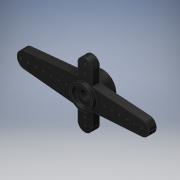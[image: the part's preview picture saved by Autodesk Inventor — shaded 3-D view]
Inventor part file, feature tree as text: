
AUTODESK INVENTOR PART (.ipt)
format: ipt  version: 2018 (Build 220112000, 112)  size: 246,784 bytes
history: native  units: in
note: dims shown in document units (in); Inventor stores cm internally (conversion verified against a paired STEP export)
features: extrude x6, sketch x6, fillet x3
ambient origin geometry x8: Origin, YZ Plane, XZ Plane, XY Plane, X Axis, Y Axis, Z Axis, Center Point
bodies: Solid1 (feature_tree)
feature tree (15):
  extrude  "Horn_Body"  Depth=0.6693in
  fillet  "Fillet1"  Radius=0.2234in
  fillet  "Fillet2"  Radius=0.2234in
  fillet  "Fillet3"  Radius=0.5118in
  extrude  "Shaft_Connector"  Depth=0.5906in
  extrude  "Shaft_Opening"  Depth=0.1969in
  extrude  "Opening_Horn_FixationScrew"  Depth=0.5906in
  extrude  "Connection_Holes"  Depth=0.6299in
  extrude  "Centering_RIng"  Depth=0.0787in TaperAngle=0.0deg
  sketch  "Sketch1"  dims[d0=0.1496in d1=0.6693in d2=0.2234in d3=0.2234in d4=0.5118in]
  sketch  "Sketch2"  dims[d5=0.1535in d8=0.5906in]
  sketch  "Sketch3"  dims[d9=0.5906in d10=0.1969in]
  sketch  "Sketch4"  dims[d11=0.1969in d12=0.5906in]
  sketch  "Sketch6"  dims[d13=0.1575in d14=0.6299in]
  sketch  "Sketch8"  dims[d15=0.6299in d16=0.0787in d17=0.0in d18=0.0748in d19=0.0748in d20=0.0787in d21=0.2795in d22=0.1496in d23=0.0748in d24=0.1063in d25=0.0in d26=0.1772in d27=0.0787in d28=0.0in d29=0.0984in d30=0.1063in d31=0.0in d35=0.1496in d36=0.0748in d37=0.0197in d38=0.0197in d39=0.0197in d41=0.0197in d42=0.0197in d43=0.1969in d44=0.0787in d46=0.0787in d47=0.0787in d48=0.0787in d49=0.0197in d50=0.0197in d51=0.0787in d52=0.0787in d53=0.0197in d54=0.0197in d55=0.0197in d56=0.0197in d57=0.0197in d58=0.1969in d59=0.0787in d60=0.0787in d61=0.0787in d62=0.0787in d63=0.0197in d64=0.0787in d65=0.0197in d66=0.0197in d67=0.0197in d68=0.0197in d69=0.1969in d70=0.0787in d71=0.1969in d72=0.0787in d73=0.0394in d74=0.0in d75=0.0529in d80=0.1969in d81=0.2441in d82=0.0394in d83=0.0in]
